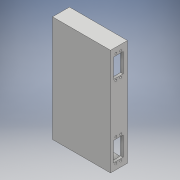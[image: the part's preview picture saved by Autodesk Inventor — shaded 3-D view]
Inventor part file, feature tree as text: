
AUTODESK INVENTOR PART (.ipt)
format: ipt  version: 2018 (Build 220112000, 112)  size: 166,912 bytes
history: native  units: mm
features: other x6, extrude x4, sketch x4
ambient origin geometry x8: Origin, YZ Plane, XZ Plane, XY Plane, X Axis, Y Axis, Z Axis, Center Point
bodies: Solid1 (feature_tree)
feature tree (14):
  other  "Blocks"
  extrude  "Extrusion1"  Depth=220.0mm
  extrude  "Extrusion2"  Depth=5.0mm
  sketch  "Sketch4"  dims[d5=5.0mm d6=5.0mm]
  sketch  "Sketch5"  dims[d7=5.0mm d8=30.0mm d9=0.0mm d10=8.0mm d11=6.0mm d12=8.0mm d13=6.0mm d14=6.0mm d15=8.0mm d16=6.0mm d17=8.0mm d18=5.0mm d19=0.0mm d20=5.0mm d21=0.0mm]
  extrude  "Extrusion3"  Depth=5.0mm
  extrude  "Extrusion4"  Depth=30.0mm TaperAngle=0.0deg
  sketch  "Sketch1"  dims[d0=120.0mm d1=220.0mm]
  sketch  "Sketch3"  dims[d2=5.0mm d3=0.0mm d4=5.0mm]
  other  "servo"
  other  "servo:1"
  other  "servo:2"
  other  "servo:3"
  other  "servo:4"
